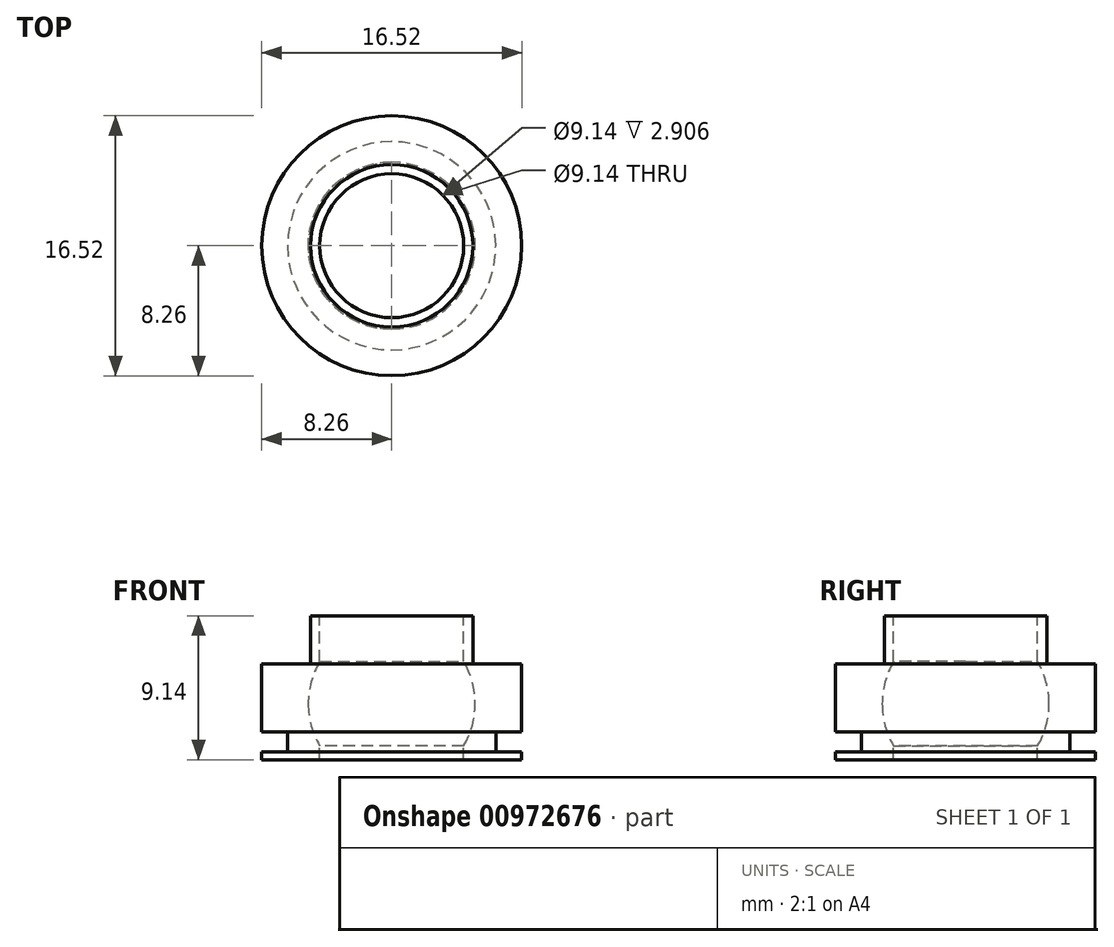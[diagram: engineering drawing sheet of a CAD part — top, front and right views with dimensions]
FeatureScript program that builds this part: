
annotation { "Feature Type Name" : "Feature", "Feature Type Description" : "" }
export const myFeature = defineFeature(function(context is Context, id is Id, definition is map)
    precondition{}
    {
        {
            var Q0;
            Q0=qCreatedBy(makeId("Top.planeOp"),FACE);
            var sketch = newSketch(context, id + "F0", { "sketchPlane" : qUnion([Q0])});
            skCircle(sketch, "E0", {"center": v(0, 0) * mm, "radius": 8.26 * mm});
            skSolve(sketch);
        }
        {
            var Q0;
            Q0=makeQuery(id+"F0.imprint","IMPRINT",FACE,{"disambiguationData":[TD([[makeQuery(id+"F0.imprint","IMPRINT",EDGE,{"derivedFrom":sQuery(id+"F0.wireOp",EDGE,"E0")}),1.0]])]});
            extrude(context, id + "F1", {"entities" : qUnion([Q0]), "depth" : 9.14 * mm, "offsetDistance" : 25.4 * mm});
        }
        {
            var Q0;
            Q0=makeQuery(id+"F1.opExtrude","CAP_FACE",FACE,{"disambiguationData":[OSD([sQuery(id+"F0.wireOp",EDGE,"E0")])],"isStart":false});
            var sketch = newSketch(context, id + "F2", { "sketchPlane" : qUnion([Q0])});
            skCircle(sketch, "E1", {"center": v(0, 0) * mm, "radius": 4.57 * mm});
            skSolve(sketch);
        }
        {
            var Q0;
            Q0=makeQuery(id+"F2.imprint","IMPRINT",FACE,{"disambiguationData":[TD([[makeQuery(id+"F2.imprint","IMPRINT",EDGE,{"derivedFrom":sQuery(id+"F2.wireOp",EDGE,"E1")}),1.0]])]});
            extrude(context, id + "F3", {"entities" : qUnion([Q0]), "operationType" : NewBodyOperationType.REMOVE, "oppositeDirection" : true, "depth" : 12.7 * mm, "offsetDistance" : 25.4 * mm});
        }
        {
            var Q0;
            Q0=qCreatedBy(makeId("Front.planeOp"),FACE);
            var sketch = newSketch(context, id + "F4", { "sketchPlane" : qUnion([Q0])});
            skLineSegment(sketch, "E2.0", {"start": v(-8.26, 9.14) * mm, "end": v(8.26, 9.14) * mm});
            skLineSegment(sketch, "E3", {"start": v(8.26, 9.4) * mm, "end": v(8.26, 0) * mm});
            skLineSegment(sketch, "E4", {"start": v(8.26, 9.14) * mm, "end": v(5.16, 9.14) * mm});
            skLineSegment(sketch, "E5", {"start": v(5.16, 9.14) * mm, "end": v(5.16, 6.1) * mm});
            skLineSegment(sketch, "E6", {"start": v(5.16, 6.1) * mm, "end": v(8.26, 6.1) * mm});
            skSolve(sketch);
        }
        {
            var Q0;
            Q0=qCreatedBy(makeId("Front.planeOp"),FACE);
            var sketch = newSketch(context, id + "F5", { "sketchPlane" : qUnion([Q0])});
            skLineSegment(sketch, "E7", {"start": v(0, 0) * mm, "end": v(0, 13.97) * mm, "construction": true});
            skSolve(sketch);
        }
        {
            var Q0;
            Q0 = qSketchRegion(id + "F4", true);
            var Q1;
            Q1=sQuery(id+"F5.wireOp",EDGE,"E7");
            revolve(context, id + "F6", {"operationType" : NewBodyOperationType.REMOVE, "surfaceOperationType" : NewSurfaceOperationType.NEW, "entities" : qUnion([Q0]), "axis" : qUnion([Q1]), "revolveType" : RevolveType.FULL, "oppositeDirection" : true});
        }
        {
            var Q0;
            Q0=qCreatedBy(makeId("Front.planeOp"),FACE);
            var sketch = newSketch(context, id + "F7", { "sketchPlane" : qUnion([Q0])});
            skLineSegment(sketch, "E8", {"start": v(8.26, 7.11) * mm, "end": v(8.26, 0) * mm});
            skLineSegment(sketch, "E9.0", {"start": v(-8.26, 0) * mm, "end": v(8.26, 0) * mm});
            skLineSegment(sketch, "E10", {"start": v(8.26, 0.5) * mm, "end": v(6.61, 0.5) * mm});
            skLineSegment(sketch, "E11", {"start": v(6.61, 0.5) * mm, "end": v(6.61, 1.78) * mm});
            skLineSegment(sketch, "E12", {"start": v(6.61, 1.78) * mm, "end": v(8.26, 1.78) * mm});
            skSolve(sketch);
        }
        {
            var Q0;
            Q0 = qSketchRegion(id + "F7", true);
            var Q1;
            Q1=sQuery(id+"F5.wireOp",EDGE,"E7");
            revolve(context, id + "F8", {"operationType" : NewBodyOperationType.REMOVE, "surfaceOperationType" : NewSurfaceOperationType.NEW, "entities" : qUnion([Q0]), "axis" : qUnion([Q1]), "revolveType" : RevolveType.FULL, "oppositeDirection" : true});
        }
        {
            var Q0;
            Q0=qCreatedBy(makeId("Right.planeOp"),FACE);
            var sketch = newSketch(context, id + "F9", { "sketchPlane" : qUnion([Q0])});
            skLineSegment(sketch, "E13", {"start": v(0, 0) * mm, "end": v(0, 3.56) * mm, "construction": true});
            skSolve(sketch);
        }
        {
            var Q0;
            Q0=qCreatedBy(makeId("Right.planeOp"),FACE);
            var sketch = newSketch(context, id + "F10", { "sketchPlane" : qUnion([Q0])});
            skLineSegment(sketch, "E14.0", {"start": v(0, 0) * mm, "end": v(0, 3.56) * mm});
            skArc(sketch, "E15", {"start": v(-5.3, 3.56) * mm, "mid": v(0, -1.74) * mm, "end": v(5.3, 3.56) * mm});
            skSolve(sketch);
        }
        {
            var Q0;
            Q0=qCreatedBy(makeId("Right.planeOp"),FACE);
            var sketch = newSketch(context, id + "F11", { "sketchPlane" : qUnion([Q0])});
            skArc(sketch, "E16.0", {"start": v(-5.3, 3.56) * mm, "mid": v(0, -1.74) * mm, "end": v(5.3, 3.56) * mm});
            skLineSegment(sketch, "E17", {"start": v(-5.3, 3.56) * mm, "end": v(5.3, 3.56) * mm});
            skSolve(sketch);
        }
        {
            var Q0;
            Q0=makeQuery(id+"F11.imprint","IMPRINT",FACE,{"disambiguationData":[TD([[makeQuery(id+"F11.imprint","IMPRINT",EDGE,{"derivedFrom":sQuery(id+"F11.wireOp",EDGE,"E16.0")}),1.0]])]});
            var Q1;
            Q1=sQuery(id+"F11.wireOp",EDGE,"E17");
            revolve(context, id + "F12", {"operationType" : NewBodyOperationType.REMOVE, "surfaceOperationType" : NewSurfaceOperationType.NEW, "entities" : qUnion([Q0]), "axis" : qUnion([Q1]), "revolveType" : RevolveType.FULL, "oppositeDirection" : true});
        }
    });
